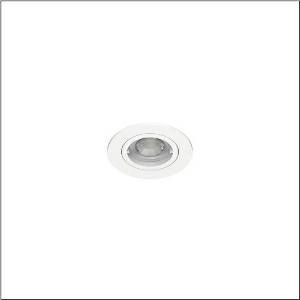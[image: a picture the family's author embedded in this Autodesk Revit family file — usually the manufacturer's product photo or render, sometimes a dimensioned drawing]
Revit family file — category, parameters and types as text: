
# Revit family: lunis_41_spot_51dt13ma31b
name_source: partatom
category: Lighting Fixtures
units: mm (PartAtom-declared; Revit-internal decimal feet)

## family parameters
Cut with Voids When Loaded = No
Host = Face
Light Source = No
Part Type = Normal
Room Calculation Point = No
Round Connector Dimension = Use Diameter
Shared = No

## types (1)
- Lunis 41 Spot (1 x LED, 560 lm, 4.6 W, 3000K)
    Apparent Load = 5 VA
    CIE Flux Codes = 87 97 99 100 100
    Color Rendering = 80
    Color Temperature = 3000K
    Default Elevation = 1800 mm
    Description = Lunis 41,  Spot, downlight, light emission: direct distribution, LED rated luminous flux: 560lm, light colour: 830, mains connection: 230V, AC, 50/60Hz, housing, round, of aluminium, coated, traffic white (RAL 9016), diameter: 88mm, recess depth: 54mm, protection rating (complete): IP20, protection rating (on room side): IP20, insulation class (complete): insulation class II (safety insulation), certification: CE, permissible ambient temperature for indoor applications: -20..+40°C, packaging unit: 1 piece
    Height = 0 mm  [stored 0 ft]
    Lamp = 1 x LED
    Lamp Light Flux = 560 lm
    Lamp Power = 4.6 W
    Lamp count = 1
    Length = 88 mm
    Luminous efficacy = 122 lm/W
    Manufacturer = Siteco
    ModVariant = No
    Model = 51DT13MA31B
    Mounting Place = Ceiling
    Mounting Type = Recessed
    Number of Poles = 1
    OnlyDefault = Yes
    Power Factor = 1
    Product Name = Lunis 41 Spot
    Product group = downlight
    ProductGroupID = 401
    Protection Class = Protection class II
    Protection Degree = IP 20
    RLX_Detail_Level = 1
    RLX_Emergency_Light_Flux = 0 lm
    RLX_Emergency_Type = 0
    RLX_Emergency_Type_DB = No
    RlxData = <blob elided: 9925 chars, md5=37e03ee6>
    Socket = socket
    Standby Power = 0 W
    System Light Flux = 560 lm
    System Power = 5 W
    Type Comments = Product without accessories
    Type Image = l_1345917.jpg
    URL = http://relux.com
    VarID = ---
    Voltage = 0 V
    Weight = 0.00 kg
    Width = 0 mm  [stored 0 ft]

note: [stored X ft] marks values corroborated as IEEE doubles in the binary element streams (Revit-internal decimal feet)

## geometry (parser evidence)
native form markers: Sweep x12
no freeform markers — native parametric forms only
